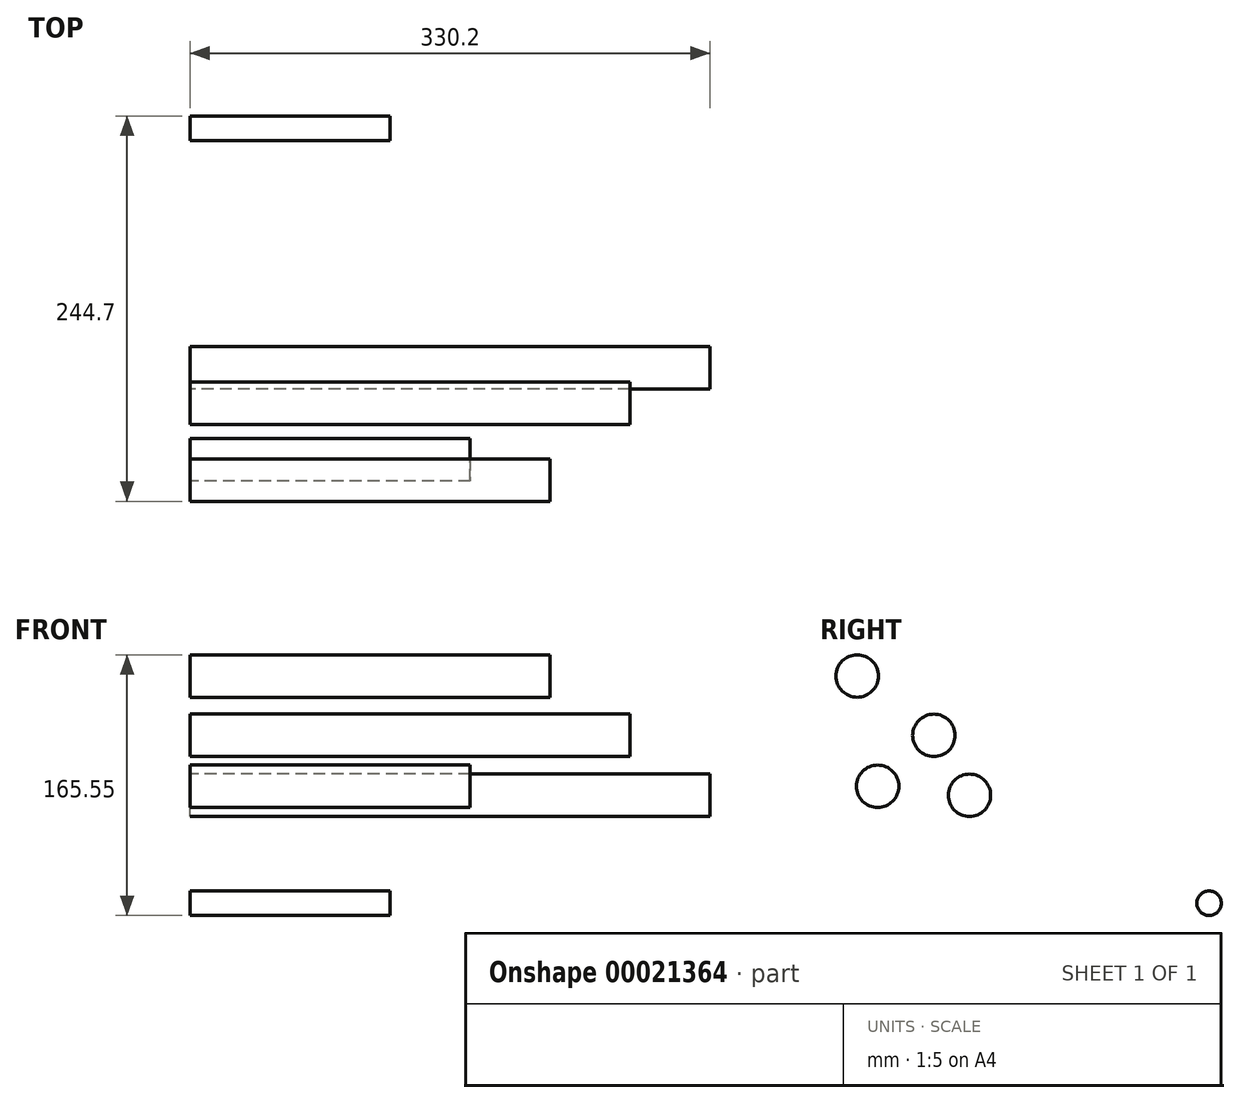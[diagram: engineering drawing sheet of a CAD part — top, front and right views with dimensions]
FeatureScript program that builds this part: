
annotation { "Feature Type Name" : "Feature", "Feature Type Description" : "" }
export const myFeature = defineFeature(function(context is Context, id is Id, definition is map)
    precondition{}
    {
        {
            var Q0;
            Q0=qCreatedBy(makeId("Right.planeOp"),FACE);
            var sketch = newSketch(context, id + "F0", { "sketchPlane" : qUnion([Q0])});
            skCircle(sketch, "E0", {"center": v(-9.2, 26.78) * mm, "radius": 13.46 * mm});
            skSolve(sketch);
        }
        {
            var Q0;
            Q0=makeQuery(id+"F0.imprint","IMPRINT",FACE,{"disambiguationData":[TD([[makeQuery(id+"F0.imprint","IMPRINT",EDGE,{"derivedFrom":sQuery(id+"F0.wireOp",EDGE,"E0")}),1.0]])]});
            extrude(context, id + "F1", {"entities" : qUnion([Q0]), "depth" : 279.4 * mm});
        }
        {
            var Q0;
            Q0=qCreatedBy(makeId("Right.planeOp"),FACE);
            var sketch = newSketch(context, id + "F2", { "sketchPlane" : qUnion([Q0])});
            skCircle(sketch, "E1", {"center": v(13.39, -11.3) * mm, "radius": 13.46 * mm});
            skSolve(sketch);
        }
        {
            var Q0;
            Q0 = qSketchRegion(id + "F2", true);
            extrude(context, id + "F3", {"entities" : qUnion([Q0]), "depth" : 330.2 * mm});
        }
        {
            var Q0;
            Q0=qCreatedBy(makeId("Right.planeOp"),FACE);
            var sketch = newSketch(context, id + "F4", { "sketchPlane" : qUnion([Q0])});
            skCircle(sketch, "E2", {"center": v(-44.9, -5.57) * mm, "radius": 13.46 * mm});
            skSolve(sketch);
        }
        {
            var Q0;
            Q0 = qSketchRegion(id + "F4", true);
            extrude(context, id + "F5", {"entities" : qUnion([Q0]), "depth" : 177.8 * mm});
        }
        {
            var Q0;
            Q0=qCreatedBy(makeId("Right.planeOp"),FACE);
            var sketch = newSketch(context, id + "F6", { "sketchPlane" : qUnion([Q0])});
            skCircle(sketch, "E3", {"center": v(-57.91, 64.48) * mm, "radius": 13.46 * mm});
            skSolve(sketch);
        }
        {
            var Q0;
            Q0 = qSketchRegion(id + "F6", true);
            extrude(context, id + "F7", {"entities" : qUnion([Q0]), "depth" : 228.6 * mm});
        }
        {
            var Q0;
            Q0=qCreatedBy(makeId("Right.planeOp"),FACE);
            var sketch = newSketch(context, id + "F8", { "sketchPlane" : qUnion([Q0])});
            skCircle(sketch, "E4", {"center": v(-65.2, -44.58) * mm, "radius": 9.92 * mm});
            skLineSegment(sketch, "E5", {"start": v(-78.1, -17.77) * mm, "end": v(-53.92, -17.77) * mm});
            skLineSegment(sketch, "E6", {"start": v(-65.2, -44.58) * mm, "end": v(-66, -17.77) * mm});
            skSolve(sketch);
        }
        {
            var Q0;
            Q0 = qSketchRegion(id + "F8", true);
            var Q1;
            Q1=sQuery(id+"F8.wireOp",EDGE,"E5");
            revolve(context, id + "F9", {"entities" : qUnion([Q0]), "axis" : qUnion([Q1]), "revolveType" : RevolveType.FULL});
        }
        {
            var Q0;
            Q0=makeQuery(id+"F9.opRevolve","SWEPT_BODY",BODY,{"disambiguationData":[OSD([sQuery(id+"F8.wireOp",EDGE,"E4")])]});
            deleteBodies(context, id + "F10", {"entities" : qUnion([Q0])});
        }
        {
            var Q0;
            Q0=qCreatedBy(makeId("Right.planeOp"),FACE);
            var sketch = newSketch(context, id + "F11", { "sketchPlane" : qUnion([Q0])});
            skCircle(sketch, "E7", {"center": v(165.58, -79.86) * mm, "radius": 7.75 * mm});
            skSolve(sketch);
        }
        {
            var Q0;
            Q0=makeQuery(id+"F11.imprint","IMPRINT",FACE,{"disambiguationData":[TD([[makeQuery(id+"F11.imprint","IMPRINT",EDGE,{"derivedFrom":sQuery(id+"F11.wireOp",EDGE,"E7")}),1.0]])]});
            extrude(context, id + "F12", {"entities" : qUnion([Q0]), "depth" : 127 * mm});
        }
    });
